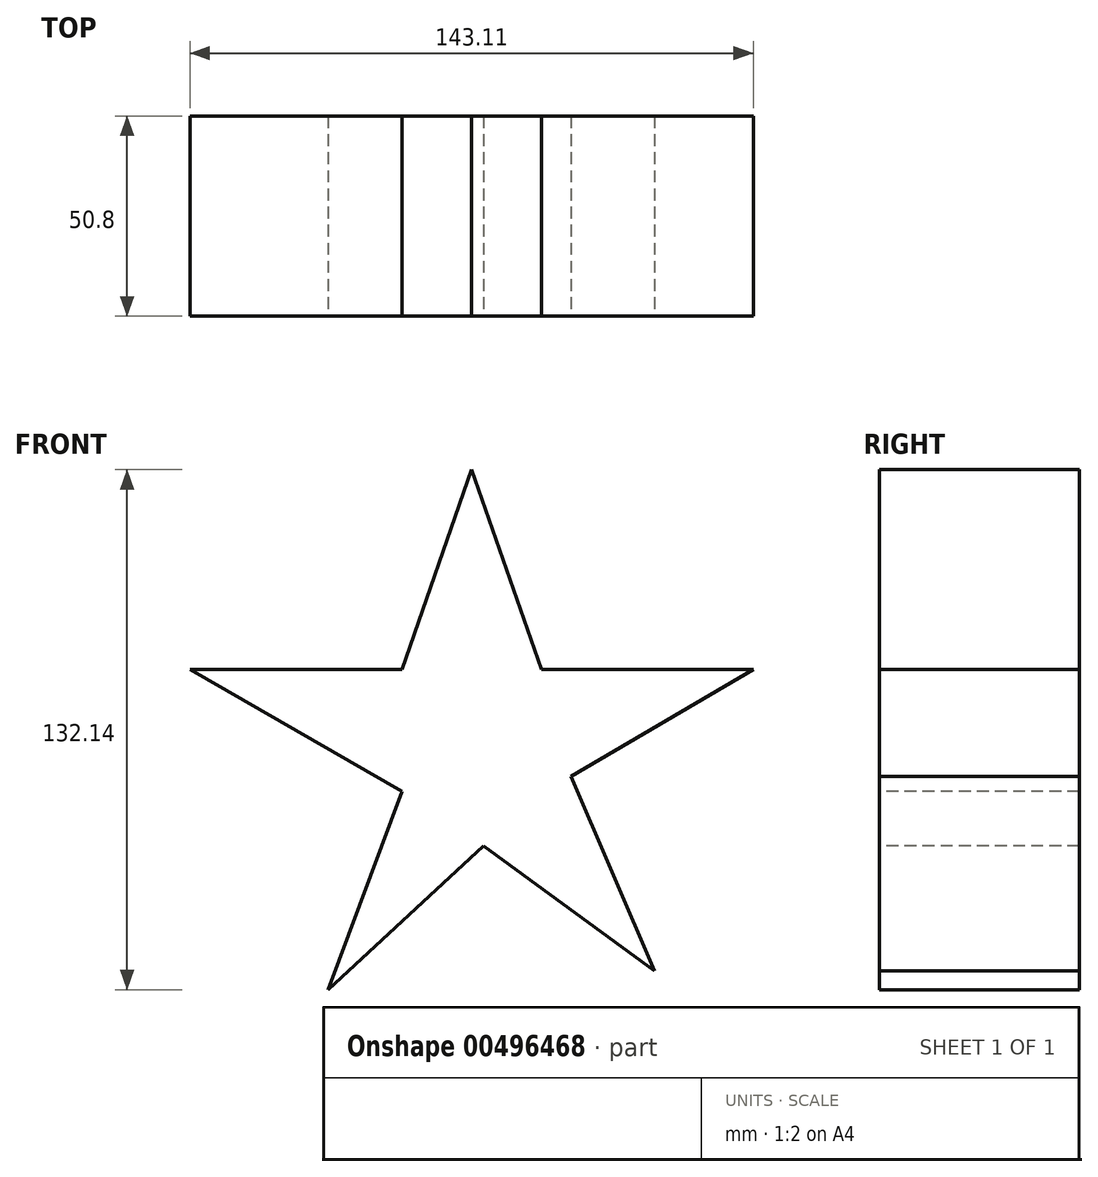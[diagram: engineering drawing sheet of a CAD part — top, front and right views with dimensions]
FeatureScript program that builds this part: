
annotation { "Feature Type Name" : "Feature", "Feature Type Description" : "" }
export const myFeature = defineFeature(function(context is Context, id is Id, definition is map)
    precondition{}
    {
        {
            var Q0;
            Q0=qCreatedBy(makeId("Front.planeOp"),FACE);
            var sketch = newSketch(context, id + "F0", { "sketchPlane" : qUnion([Q0])});
            skLineSegment(sketch, "E0", {"start": v(0, 0) * mm, "end": v(17.75, 50.78) * mm});
            skLineSegment(sketch, "E1", {"start": v(17.75, 50.78) * mm, "end": v(35.5, 0) * mm});
            skLineSegment(sketch, "E2", {"start": v(35.5, 0) * mm, "end": v(89.3, 0) * mm});
            skLineSegment(sketch, "E3", {"start": v(89.3, 0) * mm, "end": v(42.9, -27.22) * mm});
            skLineSegment(sketch, "E4", {"start": v(42.9, -27.22) * mm, "end": v(64.16, -76.64) * mm});
            skLineSegment(sketch, "E5", {"start": v(64.16, -76.64) * mm, "end": v(20.76, -44.85) * mm});
            skLineSegment(sketch, "E6", {"start": v(20.76, -44.85) * mm, "end": v(-18.75, -81.36) * mm});
            skLineSegment(sketch, "E7", {"start": v(-18.75, -81.36) * mm, "end": v(0, -30.94) * mm});
            skLineSegment(sketch, "E8", {"start": v(0, -30.94) * mm, "end": v(-53.8, 0) * mm});
            skLineSegment(sketch, "E9", {"start": v(-53.8, 0) * mm, "end": v(0, 0) * mm});
            skSolve(sketch);
        }
        {
            var Q0;
            Q0=makeQuery(id+"F0.imprint","IMPRINT",FACE,{"disambiguationData":[TD([[makeQuery(id+"F0.imprint","IMPRINT",EDGE,{"derivedFrom":sQuery(id+"F0.wireOp",EDGE,"E0")}),-1.0]])]});
            extrude(context, id + "F1", {"entities" : qUnion([Q0]), "oppositeDirection" : true, "depth" : 50.8 * mm});
        }
    });
